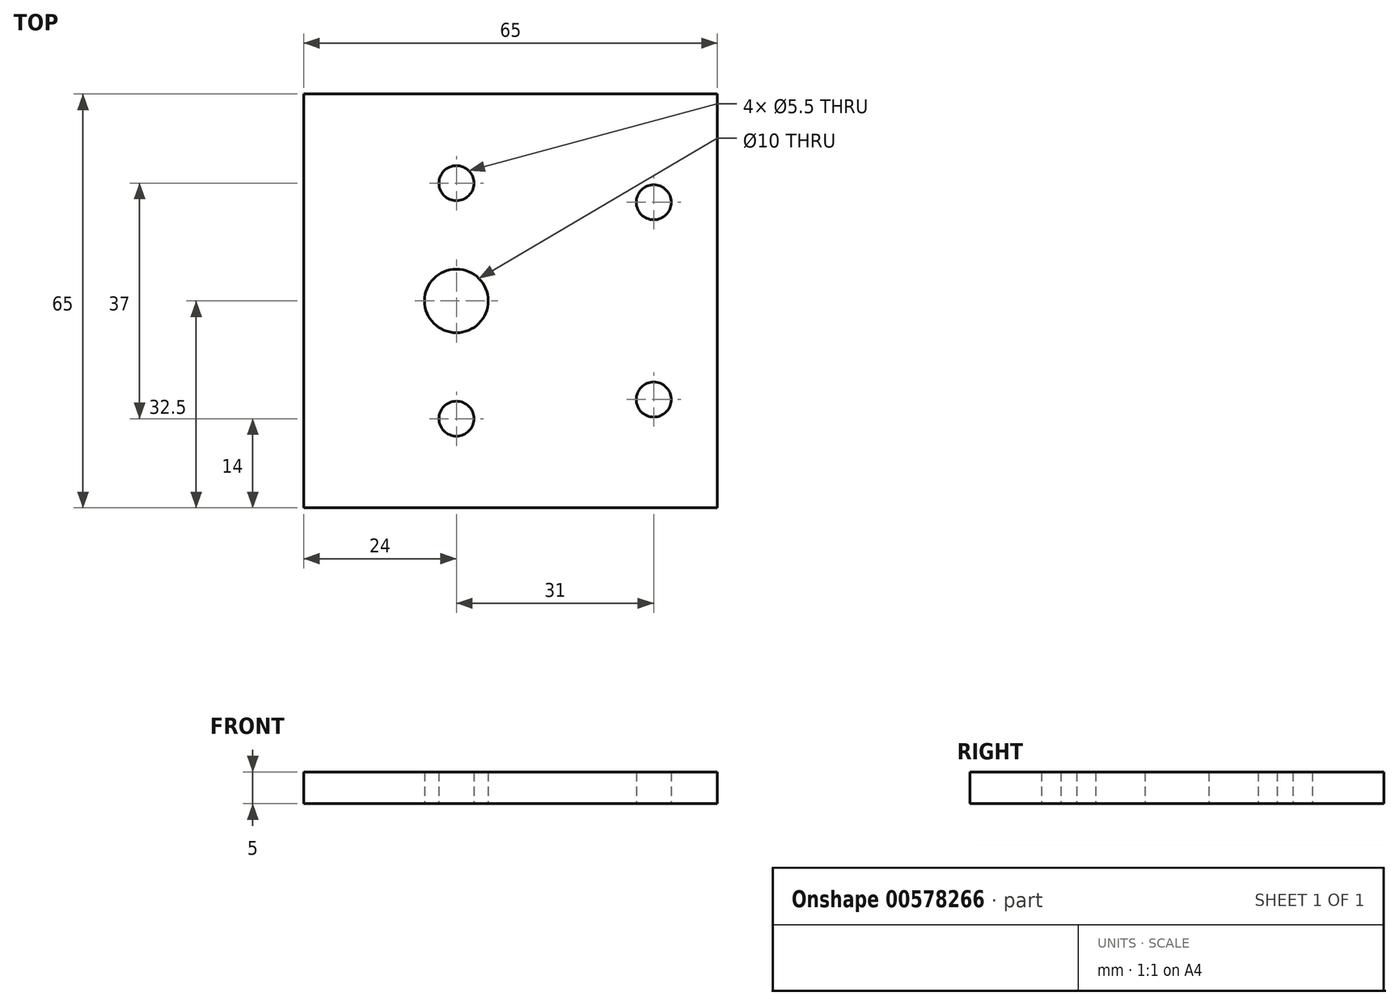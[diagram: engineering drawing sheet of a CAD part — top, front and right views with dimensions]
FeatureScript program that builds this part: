
annotation { "Feature Type Name" : "Feature", "Feature Type Description" : "" }
export const myFeature = defineFeature(function(context is Context, id is Id, definition is map)
    precondition{}
    {
        {
            var Q0;
            Q0=qCreatedBy(makeId("Front.planeOp"),FACE);
            var sketch = newSketch(context, id + "F0", { "sketchPlane" : qUnion([Q0])});
            skLineSegment(sketch, "E0.bottom", {"start": v(0, 0) * mm, "end": v(-65, 0) * mm});
            skLineSegment(sketch, "E0.top", {"start": v(0, 5) * mm, "end": v(-65, 5) * mm});
            skLineSegment(sketch, "E0.left", {"start": v(0, 0) * mm, "end": v(0, 5) * mm});
            skLineSegment(sketch, "E0.right", {"start": v(-65, 0) * mm, "end": v(-65, 5) * mm});
            skSolve(sketch);
        }
        {
            var Q0;
            Q0 = qSketchRegion(id + "F0", true);
            extrude(context, id + "F1", {"entities" : qUnion([Q0]), "oppositeDirection" : true, "depth" : 65 * mm, "offsetDistance" : 25 * mm});
        }
        {
            var Q0;
            Q0=qCreatedBy(makeId("Top.planeOp"),FACE);
            var sketch = newSketch(context, id + "F2", { "sketchPlane" : qUnion([Q0])});
            skCircle(sketch, "E1", {"center": v(-10, 48) * mm, "radius": 2.75 * mm});
            skCircle(sketch, "E2", {"center": v(-10, 17) * mm, "radius": 2.75 * mm});
            skCircle(sketch, "E3", {"center": v(-41, 51) * mm, "radius": 2.75 * mm});
            skCircle(sketch, "E4", {"center": v(-41, 14) * mm, "radius": 2.75 * mm});
            skCircle(sketch, "E5", {"center": v(-41, 32.5) * mm, "radius": 5 * mm});
            skSolve(sketch);
        }
        {
            var Q0;
            Q0 = qSketchRegion(id + "F2", true);
            extrude(context, id + "F3", {"entities" : qUnion([Q0]), "operationType" : NewBodyOperationType.REMOVE, "depth" : 5 * mm, "offsetDistance" : 25 * mm});
        }
    });
